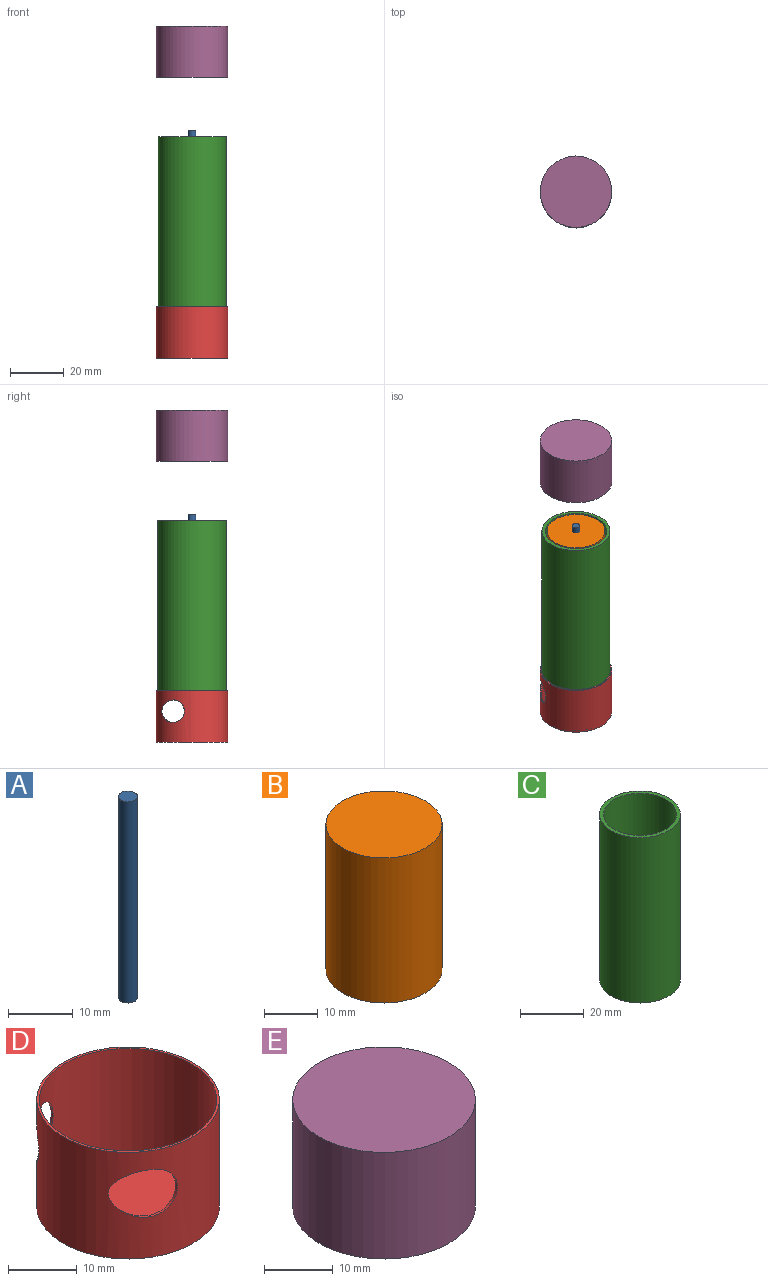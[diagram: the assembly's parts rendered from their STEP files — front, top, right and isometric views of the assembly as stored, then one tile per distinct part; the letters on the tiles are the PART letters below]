
ASSEMBLY  parts=5 mates=4
PART A: 3 faces, bbox 2.9x2.9x38.1 mm
  f0: cylinder r=1.46mm len=38.1mm, axis (0,0,-1), area 348.6mm2, adj f1,f2
  f1: plane 2.91x2.91mm, normal (0,0,1), area 6.7mm2, adj f0
  f2: plane 2.91x2.91mm, normal (0,0,-1), area 6.7mm2, adj f0
PART B: 3 faces, bbox 21.6x21.6x33 mm
  f0: cylinder r=10.79mm len=33.02mm, axis (0,0,-1), area 2239.6mm2, adj f1,f2
  f1: plane 21.59x21.59mm, normal (0,0,1), area 366.1mm2, adj f0
  f2: plane 21.59x21.59mm, normal (0,0,-1), area 366.1mm2, adj f0
PART C: 4 faces, bbox 25.4x25.4x63.5 mm
  f0: cylinder r=12.7mm len=63.5mm, axis (0,0,-1), area 5067.1mm2, adj f1,f2
  f1: plane 25.4x25.4mm, normal (0,0,1), area 96.3mm2, adj f0,f3
  f2: plane 25.4x25.4mm, normal (0,0,-1), area 96.3mm2, adj f0,f3
  f3: cylinder r=11.43mm len=63.5mm, axis (0,0,1), area 4560.4mm2, adj f1,f2
PART D: 7 faces, bbox 26.7x26.7x19.1 mm
  f0: cylinder r=13.33mm len=26.67mm, axis (0,0,-1), area 1458.8mm2, adj f2,f3,f5,f6
  f1: cylinder r=12.95mm len=25.91mm, axis (0,0,1), area 1359.2mm2, adj f2,f4,f5,f6
  f2: plane 26.67x26.67mm, normal (0,0,1), area 31.5mm2, adj f0,f1
  f3: plane 26.67x26.67mm, normal (0,0,-1), area 558.6mm2, adj f0
  f4: plane 25.91x25.91mm, normal (0,0,1), area 527.2mm2, adj f1
  f5: cylinder r=4.21mm len=8.42mm, axis (0,1,0), area 13.3mm2, adj f0,f1
  f6: cylinder r=4.21mm len=8.42mm, axis (0,1,0), area 13.3mm2, adj f0,f1
PART E: 5 faces, bbox 26.7x26.7x19.1 mm
  f0: cylinder r=13.33mm len=26.67mm, axis (0,0,-1), area 1596.1mm2, adj f1,f2
  f1: plane 26.67x26.67mm, normal (0,0,1), area 558.6mm2, adj f0
  f2: plane 26.67x26.67mm, normal (0,0,-1), area 31.5mm2, adj f0,f3
  f3: cylinder r=12.95mm len=25.91mm, axis (0,0,-1), area 1447.2mm2, adj f2,f4
  f4: plane 25.91x25.91mm, normal (0,0,-1), area 527.2mm2, adj f3
PLACE A rot(axis=(0,0,-1),26.3deg) t=(-96.69,-31.79,18.95)mm
PLACE B rot(axis=(0,0,-1),26.3deg) t=(-42.77,-86.3,21.49)mm
PLACE C t=(-55.78,-32.63,-8.94)mm fixed
PLACE D rot(axis=(0,0,-1),90deg) t=(-20.27,-3.52,-27.99)mm
PLACE E rot(axis=(0,0,1),90deg) t=(-97.43,-2.97,76.9)mm
MATE revolute D.f0 <-> C.f0  axis (0,0,1) through (-55.78,-32.63,-8.94)mm
MATE fastened B.f0 <-> A.f0  axis (0,0,-1) through (-55.78,-32.63,38)mm
MATE slider E.f0 <-> C.f0  axis (0,0,-1) through (-55.78,-32.63,76.9)mm
MATE cylindrical A.f0 <-> D.f0  axis (0,0,-1) through (-55.78,-32.63,18.95)mm
